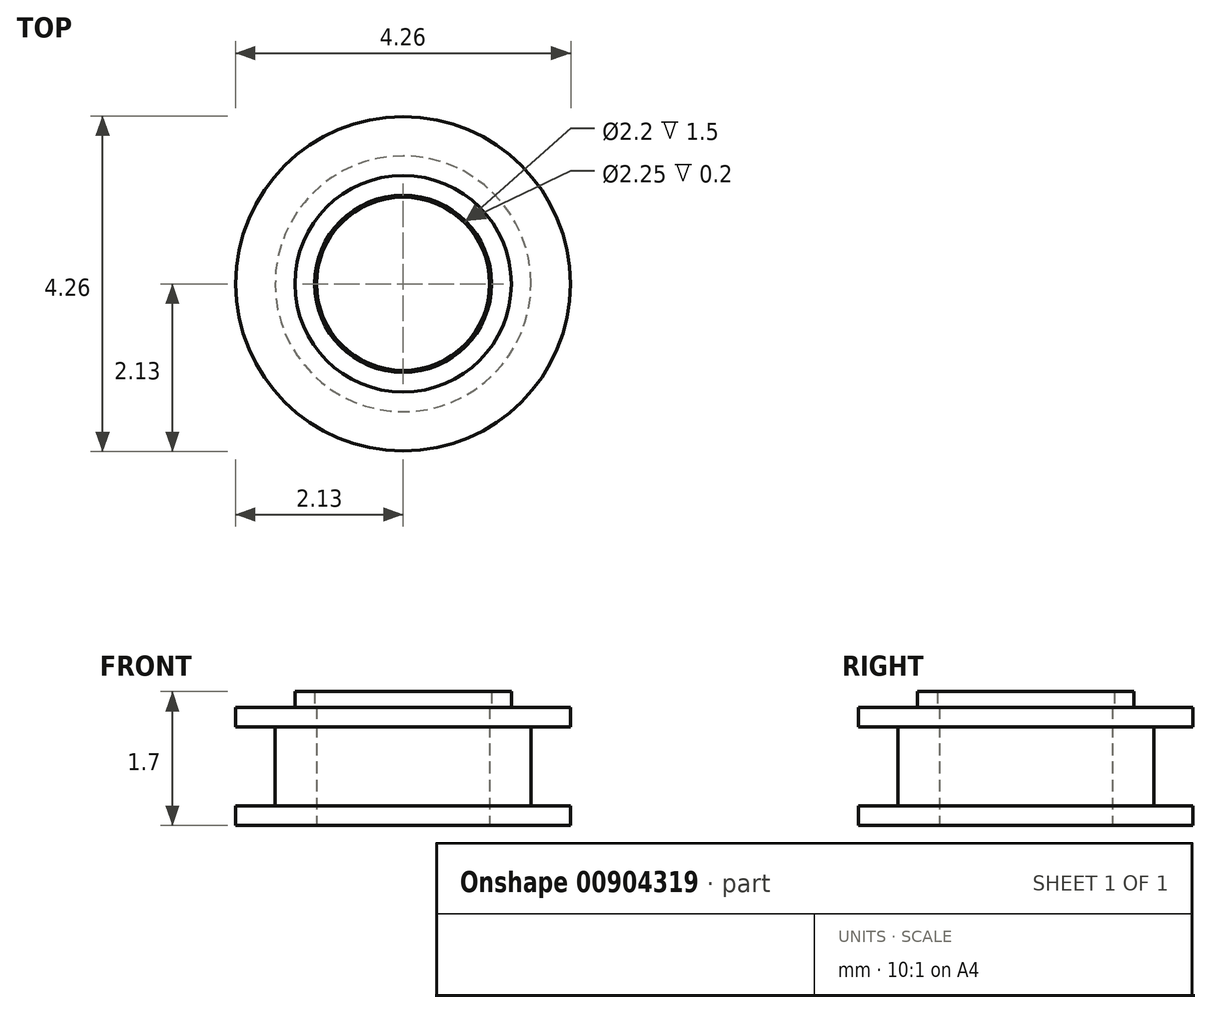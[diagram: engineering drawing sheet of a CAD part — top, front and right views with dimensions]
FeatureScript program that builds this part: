
annotation { "Feature Type Name" : "Feature", "Feature Type Description" : "" }
export const myFeature = defineFeature(function(context is Context, id is Id, definition is map)
    precondition{}
    {
        {
            var Q0;
            Q0=qCreatedBy(makeId("Front.planeOp"),FACE);
            var sketch = newSketch(context, id + "F0", { "sketchPlane" : qUnion([Q0])});
            skLineSegment(sketch, "E0.bottom", {"start": v(0, 0) * mm, "end": v(-1.1, 0) * mm});
            skLineSegment(sketch, "E0.top", {"start": v(0, 1.5) * mm, "end": v(-1.1, 1.5) * mm});
            skLineSegment(sketch, "E0.left", {"start": v(0, 0) * mm, "end": v(0, 1.5) * mm});
            skLineSegment(sketch, "E0.right", {"start": v(-1.1, 0) * mm, "end": v(-1.1, 1.5) * mm});
            skLineSegment(sketch, "E1.bottom", {"start": v(-1.1, 1.5) * mm, "end": v(-1.13, 1.5) * mm});
            skLineSegment(sketch, "E1.top", {"start": v(-1.1, 0) * mm, "end": v(-1.12, 0) * mm});
            skLineSegment(sketch, "E1.left", {"start": v(-1.1, 1.5) * mm, "end": v(-1.1, 0) * mm});
            skLineSegment(sketch, "E1.right", {"start": v(-1.13, 1.5) * mm, "end": v(-1.12, 0) * mm});
            skLineSegment(sketch, "E2.bottom", {"start": v(-1.13, 1.5) * mm, "end": v(-1.38, 1.5) * mm});
            skLineSegment(sketch, "E2.top", {"start": v(-1.13, 0) * mm, "end": v(-1.38, 0) * mm});
            skLineSegment(sketch, "E2.left", {"start": v(-1.13, 1.5) * mm, "end": v(-1.13, 0) * mm});
            skLineSegment(sketch, "E2.right", {"start": v(-1.38, 1.5) * mm, "end": v(-1.38, 0) * mm});
            skLineSegment(sketch, "E3.top", {"start": v(-1.13, 1.7) * mm, "end": v(-1.38, 1.7) * mm});
            skLineSegment(sketch, "E3.left", {"start": v(-1.13, 1.5) * mm, "end": v(-1.13, 1.7) * mm});
            skLineSegment(sketch, "E3.right", {"start": v(-1.38, 1.5) * mm, "end": v(-1.38, 1.7) * mm});
            skLineSegment(sketch, "E4.bottom", {"start": v(-1.38, 0) * mm, "end": v(-1.12, 0) * mm});
            skLineSegment(sketch, "E4.top", {"start": v(-1.37, -0.2) * mm, "end": v(-1.12, -0.2) * mm});
            skLineSegment(sketch, "E4.left", {"start": v(-1.38, 0) * mm, "end": v(-1.38, -0.2) * mm});
            skLineSegment(sketch, "E4.right", {"start": v(-1.12, 0) * mm, "end": v(-1.12, -0.2) * mm});
            skLineSegment(sketch, "E5.bottom", {"start": v(-1.38, 1.5) * mm, "end": v(-2.13, 1.5) * mm});
            skLineSegment(sketch, "E5.top", {"start": v(-1.38, 0) * mm, "end": v(-2.12, 0) * mm});
            skLineSegment(sketch, "E5.right", {"start": v(-2.13, 1.5) * mm, "end": v(-2.12, 0) * mm});
            skLineSegment(sketch, "E6.bottom", {"start": v(-2.12, 1.25) * mm, "end": v(-1.63, 1.25) * mm});
            skLineSegment(sketch, "E6.top", {"start": v(-2.12, 0.25) * mm, "end": v(-1.63, 0.25) * mm});
            skLineSegment(sketch, "E6.left", {"start": v(-2.12, 1.25) * mm, "end": v(-2.12, 0.25) * mm});
            skLineSegment(sketch, "E6.right", {"start": v(-1.63, 1.25) * mm, "end": v(-1.63, 0.25) * mm});
            skSolve(sketch);
        }
        {
            var Q0;
            Q0=makeQuery(id+"F0.imprint","IMPRINT",FACE,{"disambiguationData":[TD([[makeQuery(id+"F0.imprint","IMPRINT",EDGE,{"derivedFrom":sQuery(id+"F0.wireOp",EDGE,"E1.bottom")}),1.0]])]});
            var Q1;
            Q1=makeQuery(id+"F0.imprint","IMPRINT",FACE,{"disambiguationData":[TD([[makeQuery(id+"F0.imprint","IMPRINT",EDGE,{"derivedFrom":sQuery(id+"F0.wireOp",EDGE,"E2.left")}),-1.0]])]});
            var Q2;
            Q2=makeQuery(id+"F0.imprint","IMPRINT",FACE,{"disambiguationData":[TD([[makeQuery(id+"F0.imprint","IMPRINT",EDGE,{"derivedFrom":sQuery(id+"F0.wireOp",EDGE,"E2.bottom")}),-1.0]])]});
            var Q3;
            Q3=makeQuery(id+"F0.imprint","IMPRINT",FACE,{"disambiguationData":[TD([[makeQuery(id+"F0.imprint","IMPRINT",EDGE,{"derivedFrom":sQuery(id+"F0.wireOp",EDGE,"E4.bottom")}),-1.0]])]});
            var Q4;
            {var subQ1=sQuery(id+"F0.wireOp",EDGE,"E5.bottom");Q4=makeQuery(id+"F0.imprint","IMPRINT",FACE,{"disambiguationData":[TD([[makeQuery(id+"F0.imprint","IMPRINT",EDGE,{"derivedFrom":subQ1}),1.0]])]});}
            var Q5;
            Q5=sQuery(id+"F0.wireOp",EDGE,"E0.left");
            revolve(context, id + "F1", {"surfaceOperationType" : NewSurfaceOperationType.NEW, "entities" : qUnion([Q0, Q1, Q2, Q3, Q4]), "axis" : qUnion([Q5]), "revolveType" : RevolveType.FULL});
        }
    });
